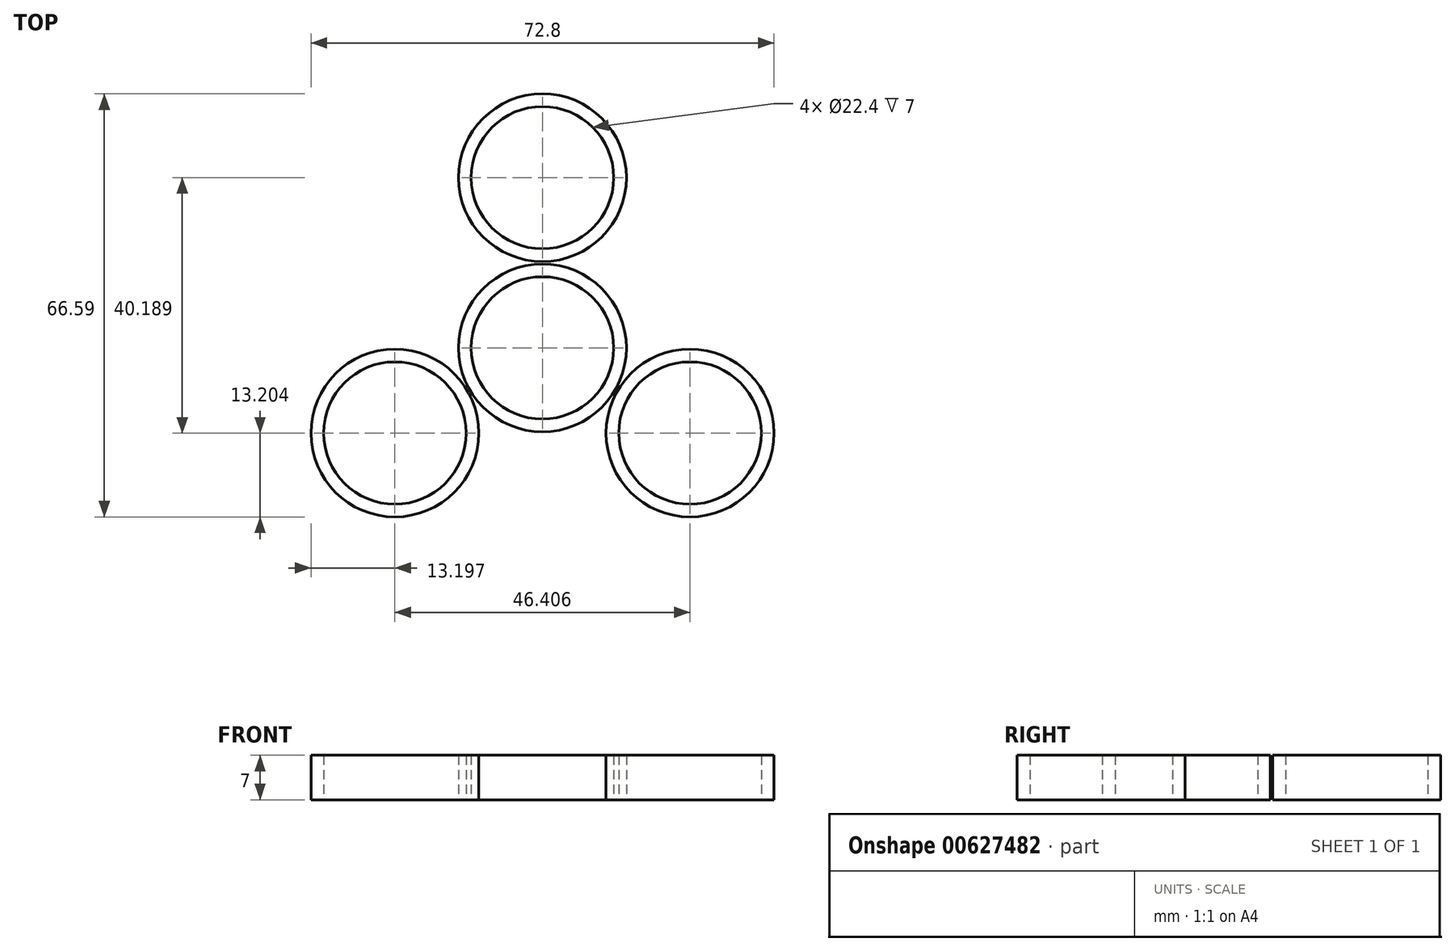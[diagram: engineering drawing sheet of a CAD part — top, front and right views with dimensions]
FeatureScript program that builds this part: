
annotation { "Feature Type Name" : "Feature", "Feature Type Description" : "" }
export const myFeature = defineFeature(function(context is Context, id is Id, definition is map)
    precondition{}
    {
        {
            var Q0;
            Q0=qCreatedBy(makeId("Top.planeOp"),FACE);
            var sketch = newSketch(context, id + "F0", { "sketchPlane" : qUnion([Q0])});
            skCircle(sketch, "E0", {"center": v(0, 0) * mm, "radius": 11.2 * mm});
            skCircle(sketch, "E1", {"center": v(0, 0) * mm, "radius": 13.2 * mm});
            skCircle(sketch, "E2", {"center": v(0, 26.8) * mm, "radius": 11.2 * mm});
            skCircle(sketch, "E3", {"center": v(0, 26.8) * mm, "radius": 13.2 * mm});
            skCircle(sketch, "E4.1.0", {"center": v(-23.2, -13.4) * mm, "radius": 11.2 * mm});
            skCircle(sketch, "E4.1.1", {"center": v(-23.2, -13.4) * mm, "radius": 13.2 * mm});
            skCircle(sketch, "E4.2.0", {"center": v(23.2, -13.4) * mm, "radius": 11.2 * mm});
            skCircle(sketch, "E4.2.1", {"center": v(23.2, -13.4) * mm, "radius": 13.2 * mm});
            skArc(sketch, "E5", {"start": v(-19.69, 0) * mm, "mid": v(-11.23, 7.03) * mm, "end": v(-9.8, 17.94) * mm});
            skArc(sketch, "E6.1.0", {"start": v(9.84, -17.05) * mm, "mid": v(-0.48, -13.24) * mm, "end": v(-10.64, -17.45) * mm});
            skArc(sketch, "E6.2.0", {"start": v(9.84, 17.05) * mm, "mid": v(11.7, 6.2) * mm, "end": v(20.43, -0.5) * mm});
            skSolve(sketch);
        }
        {
            var Q0;
            Q0 = qSketchRegion(id + "F0", true);
            extrude(context, id + "F1", {"entities" : qUnion([Q0]), "depth" : 7 * mm, "offsetDistance" : 25 * mm});
        }
        {
            var Q0;
            Q0=sQuery(id+"F0.wireOp",EDGE,"E5");
            extrude(context, id + "F2", {"bodyType" : ToolBodyType.SURFACE, "surfaceEntities" : qUnion([Q0]), "depth" : 7 * mm, "offsetDistance" : 25 * mm});
        }
        {
            var Q0;
            Q0=sQuery(id+"F0.wireOp",EDGE,"E6.2.0");
            extrude(context, id + "F3", {"bodyType" : ToolBodyType.SURFACE, "surfaceEntities" : qUnion([Q0]), "depth" : 7 * mm, "offsetDistance" : 25 * mm});
        }
        {
            var Q0;
            Q0=sQuery(id+"F0.wireOp",EDGE,"E6.1.0");
            extrude(context, id + "F4", {"bodyType" : ToolBodyType.SURFACE, "surfaceEntities" : qUnion([Q0]), "depth" : 7 * mm, "offsetDistance" : 25 * mm});
        }
    });
